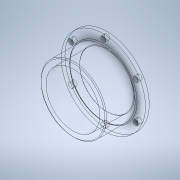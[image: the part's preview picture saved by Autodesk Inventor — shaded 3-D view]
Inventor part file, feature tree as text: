
AUTODESK INVENTOR PART (.ipt)
format: ipt  version: 2021.2 (Build 252289000, 289)  size: 163,328 bytes
history: native  units: mm
features: sketch x5, extrude x2, hole x2, chamfer x2, other x1, fillet x1
ambient origin geometry x8: Origin, YZ Plane, XZ Plane, XY Plane, X Axis, Y Axis, Z Axis, Center Point
bodies: Body1 (feature_tree)
feature tree (13):
  other  "Твердое тело1"
  extrude  "Выдавливание1"  Depth=180.0mm
  sketch  "Эскиз2"
  sketch  "Эскиз3"
  extrude  "Выдавливание2"  Depth=8.0mm TaperAngle=0.0deg
  hole  "Отверстие1"  [1 undecoded]
  chamfer  "Фаска1"  Distance=140.0mm
  chamfer  "Фаска2"  Distance=65.0mm
  fillet  "Сопряжение1"  Radius=2.0mm
  hole  "Отверстие2"  [1 undecoded]
  sketch  "Эскиз1"
  sketch  "Эскиз4"
  sketch  "Эскиз5"
note: 2 required parameter values undecoded (feature->parameter linkage not recoverable at this tier; creation-order binding heuristic only, values carry confidence <= 0.55)
